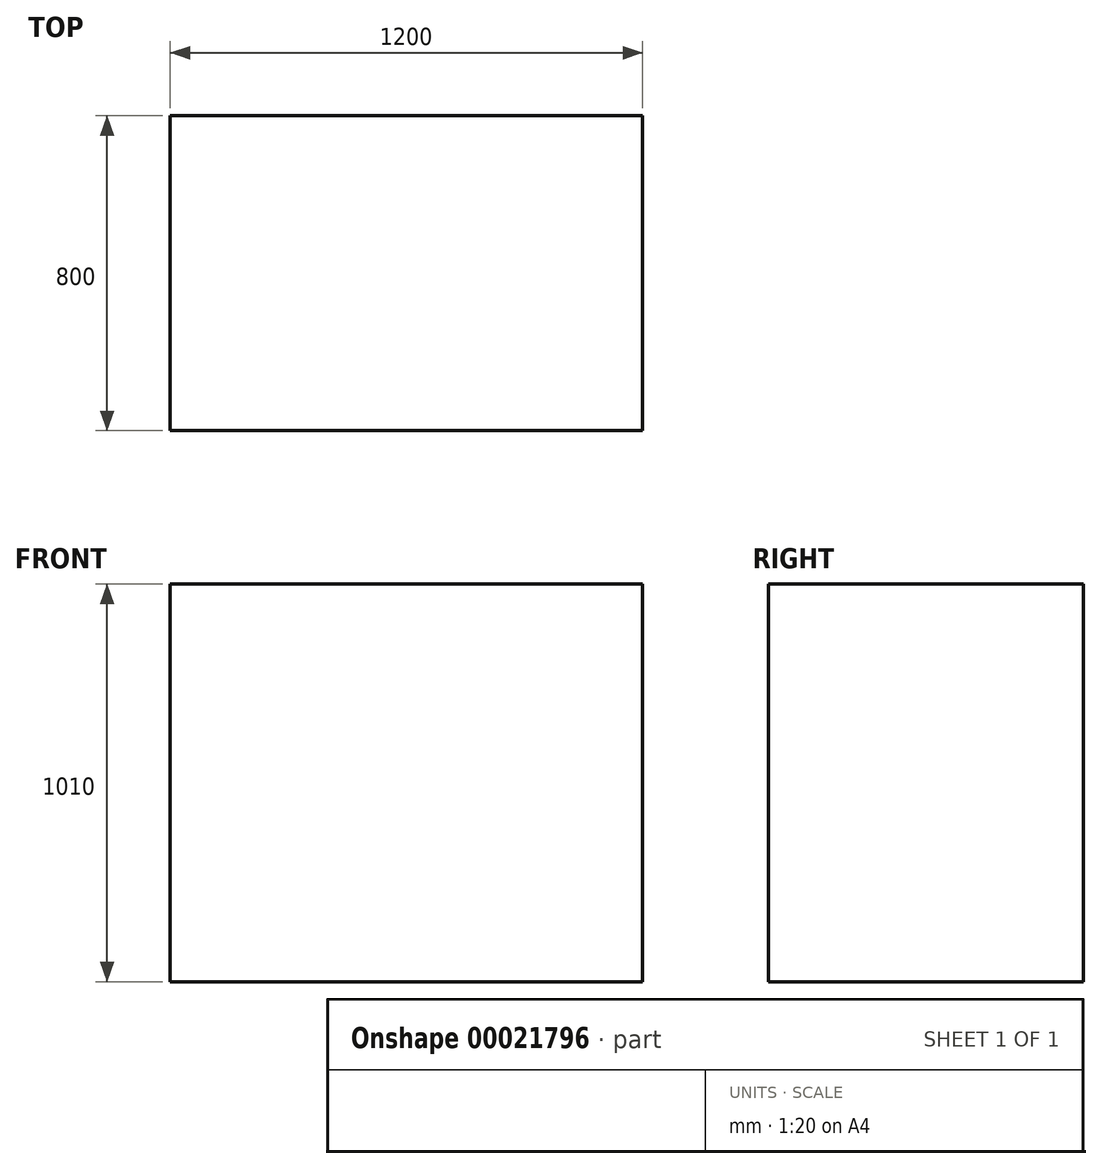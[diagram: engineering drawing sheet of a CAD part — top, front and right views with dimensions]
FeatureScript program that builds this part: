
annotation { "Feature Type Name" : "Feature", "Feature Type Description" : "" }
export const myFeature = defineFeature(function(context is Context, id is Id, definition is map)
    precondition{}
    {
        {
            var Q0;
            Q0=qCreatedBy(makeId("Top.planeOp"),FACE);
            var sketch = newSketch(context, id + "F0", { "sketchPlane" : qUnion([Q0])});
            skLineSegment(sketch, "E0.bottom", {"start": v(0, 0) * mm, "end": v(1200, 0) * mm});
            skLineSegment(sketch, "E0.top", {"start": v(0, 800) * mm, "end": v(1200, 800) * mm});
            skLineSegment(sketch, "E0.left", {"start": v(0, 0) * mm, "end": v(0, 800) * mm});
            skLineSegment(sketch, "E0.right", {"start": v(1200, 0) * mm, "end": v(1200, 800) * mm});
            skSolve(sketch);
        }
        {
            var Q0;
            Q0=makeQuery(id+"F0.imprint","IMPRINT",FACE,{"disambiguationData":[TD([[makeQuery(id+"F0.imprint","IMPRINT",EDGE,{"derivedFrom":sQuery(id+"F0.wireOp",EDGE,"E0.bottom")}),1.0]])]});
            extrude(context, id + "F1", {"entities" : qUnion([Q0]), "depth" : 1010 * mm});
        }
    });
